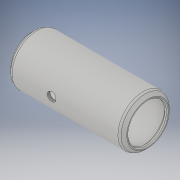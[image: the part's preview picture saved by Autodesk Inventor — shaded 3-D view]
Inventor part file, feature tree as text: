
AUTODESK INVENTOR PART (.ipt)
format: ipt  version: 2018 (Build 220112000, 112)  size: 189,440 bytes
history: native  units: in
note: dims shown in document units (in); Inventor stores cm internally (conversion verified against a paired STEP export)
features: other x42, sketch x2, revolve x1, extrude x1
ambient origin geometry x8: Origin, YZ Plane, XZ Plane, XY Plane, X Axis, Y Axis, Z Axis, Center Point
bodies: Solid1 (feature_tree)
feature tree (46):
  revolve  "Revolution1"  [1 undecoded]
  extrude  "Extrusion1"  [1 undecoded]
  other  "cp1_XY"
  other  "cp1_YZ"
  other  "cp1_ZX"
  other  "cp1_X"
  other  "cp1_Y"
  other  "cp1_Z"
  other  "cp1_Center"
  other  "cp2_XY"
  other  "cp2_YZ"
  other  "cp2_ZX"
  other  "cp2_X"
  other  "cp2_Y"
  other  "cp2_Z"
  other  "cp2_Center"
  other  "cp3_XY"
  other  "cp3_YZ"
  other  "cp3_ZX"
  other  "cp3_X"
  other  "cp3_Y"
  other  "cp3_Z"
  other  "cp3_Center"
  other  "cp4_XY"
  other  "cp4_YZ"
  other  "cp4_ZX"
  other  "cp4_X"
  other  "cp4_Y"
  other  "cp4_Z"
  other  "cp4_Center"
  other  "tube_front_XY"
  other  "tube_front_YZ"
  other  "tube_front_ZX"
  other  "tube_front_X"
  other  "tube_front_Y"
  other  "tube_front_Z"
  other  "tube_front_Center"
  other  "tube_rear_XY"
  other  "tube_rear_YZ"
  other  "tube_rear_ZX"
  other  "tube_rear_X"
  other  "tube_rear_Y"
  other  "tube_rear_Z"
  other  "tube_rear_Center"
  sketch  "Sketch_1"  dims[d0=360.0deg d1=0.1795in d2=0.0in]
  sketch  "Sketch_4"
note: 2 required parameter values undecoded (feature->parameter linkage not recoverable at this tier; creation-order binding heuristic only, values carry confidence <= 0.55)